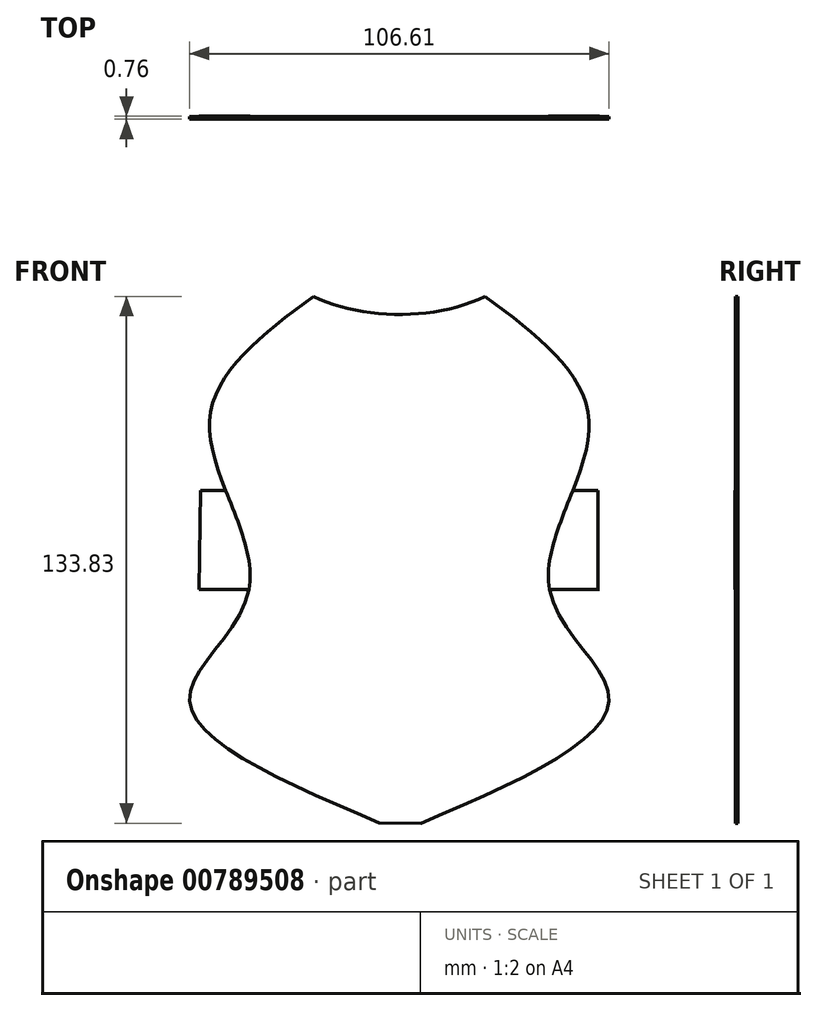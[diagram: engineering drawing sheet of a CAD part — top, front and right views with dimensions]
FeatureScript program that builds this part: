
annotation { "Feature Type Name" : "Feature", "Feature Type Description" : "" }
export const myFeature = defineFeature(function(context is Context, id is Id, definition is map)
    precondition{}
    {
        {
            var Q0;
            Q0=qCreatedBy(makeId("Front.planeOp"),FACE);
            var sketch = newSketch(context, id + "F0", { "sketchPlane" : qUnion([Q0])});
            skFitSpline(sketch, "E0", {"points": [v(-22.9, 56.25) * mm, v(-49.32, 23.98) * mm, v(-39.24, -18.18) * mm, v(-54.37, -46.01) * mm, v(-6.16, -77.48) * mm], "startDerivative": vector(-159, -118.8) * mm, "endDerivative": vector(249.85, -106.1) * mm});
            skFitSpline(sketch, "E1.MirrorCS", {"points": [v(20.78, 56.25) * mm, v(47.2, 23.98) * mm, v(37.11, -18.18) * mm, v(52.24, -46.01) * mm, v(4.44, -77.58) * mm], "startDerivative": vector(159, -118.8) * mm, "endDerivative": vector(-249.85, -106.1) * mm});
            skLineSegment(sketch, "E2", {"start": v(-6.16, -77.48) * mm, "end": v(4.44, -77.58) * mm});
            skFitSpline(sketch, "E3", {"points": [v(-22.9, 56.25) * mm, v(20.78, 56.25) * mm], "startDerivative": vector(37.1, -17.96) * mm, "endDerivative": vector(38.92, 18.68) * mm});
            skLineSegment(sketch, "E4", {"start": v(43.03, 6.99) * mm, "end": v(49.38, 6.99) * mm});
            skLineSegment(sketch, "E5", {"start": v(37.11, -18.18) * mm, "end": v(49.81, -18.18) * mm});
            skLineSegment(sketch, "E6", {"start": v(49.38, 6.99) * mm, "end": v(49.38, -18.15) * mm});
            skLineSegment(sketch, "E7", {"start": v(49.81, -18.18) * mm, "end": v(49.38, -18.15) * mm});
            skLineSegment(sketch, "E8", {"start": v(43.03, 6.99) * mm, "end": v(-45.15, 6.99) * mm});
            skLineSegment(sketch, "E9", {"start": v(-45.15, 6.99) * mm, "end": v(-51.5, 6.99) * mm});
            skLineSegment(sketch, "E10", {"start": v(37.11, -18.18) * mm, "end": v(-51.94, -18.18) * mm});
            skLineSegment(sketch, "E11", {"start": v(-51.5, 6.99) * mm, "end": v(-51.94, -18.18) * mm});
            skSolve(sketch);
        }
        {
            var Q0;
            Q0=makeQuery(id+"F0.imprint","IMPRINT",FACE,{"disambiguationData":[TD([[makeQuery(id+"F0.imprint","IMPRINT",EDGE,{"derivedFrom":sQuery(id+"F0.wireOp",EDGE,"E0")}),1.0]])]});
            extrude(context, id + "F1", {"entities" : qUnion([Q0]), "endBound" : BoundingType.SYMMETRIC, "depth" : 0.64 * mm, "offsetDistance" : 25.4 * mm});
        }
        {
            var Q0;
            {var subQ0=sQuery(id+"F0.wireOp",EDGE,"E9");Q0=makeQuery(id+"F0.imprint","IMPRINT",FACE,{"disambiguationData":[TD([[makeQuery(id+"F0.imprint","IMPRINT",EDGE,{"derivedFrom":subQ0}),1.0]])]});}
            var Q1;
            {var subQ0=sQuery(id+"F0.wireOp",EDGE,"E4");Q1=makeQuery(id+"F0.imprint","IMPRINT",FACE,{"disambiguationData":[TD([[makeQuery(id+"F0.imprint","IMPRINT",EDGE,{"derivedFrom":subQ0}),-1.0]])]});}
            extrude(context, id + "F2", {"entities" : qUnion([Q0, Q1]), "operationType" : NewBodyOperationType.ADD, "endBound" : BoundingType.SYMMETRIC, "depth" : 0.76 * mm, "offsetDistance" : 25.4 * mm});
        }
    });
